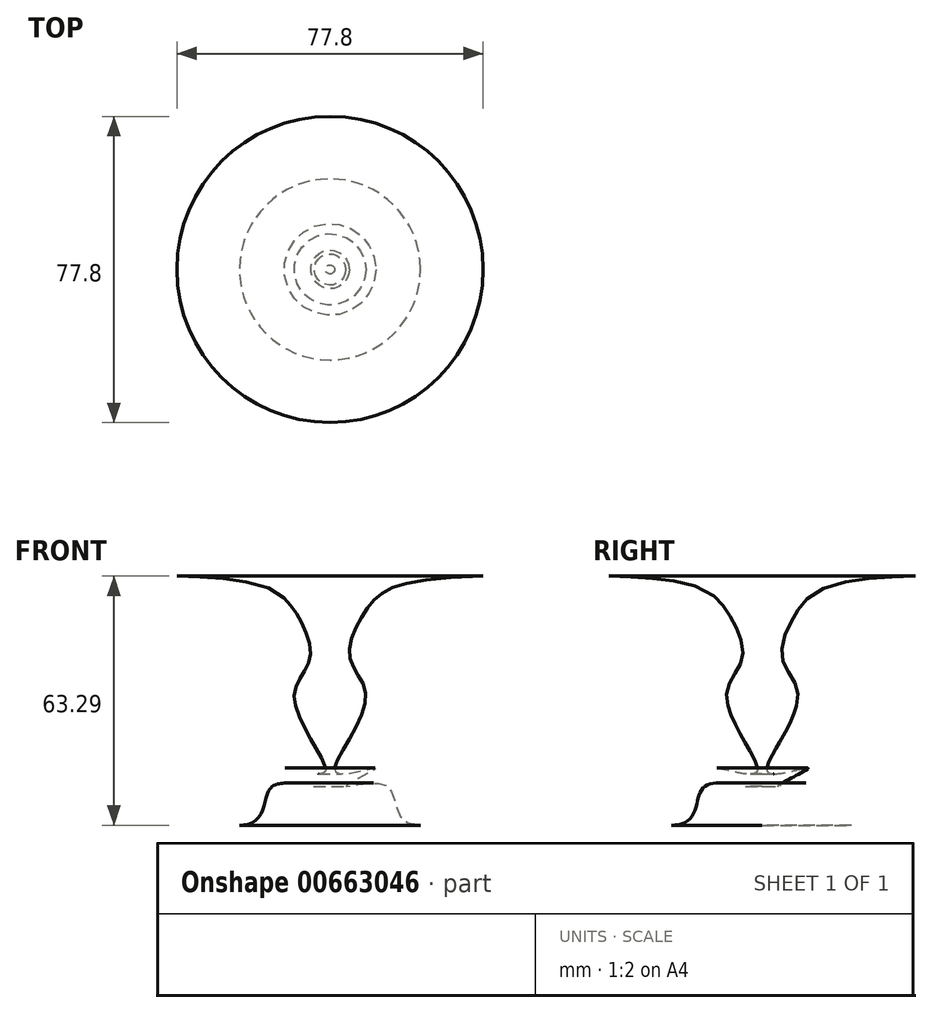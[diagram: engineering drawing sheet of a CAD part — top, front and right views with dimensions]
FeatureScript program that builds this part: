
annotation { "Feature Type Name" : "Feature", "Feature Type Description" : "" }
export const myFeature = defineFeature(function(context is Context, id is Id, definition is map)
    precondition{}
    {
        {
            var Q0;
            Q0=qCreatedBy(makeId("Front.planeOp"),FACE);
            var sketch = newSketch(context, id + "F0", { "sketchPlane" : qUnion([Q0])});
            skFitSpline(sketch, "E0", {"points": [v(38.9, 63.3) * mm, v(9.07, 54.53) * mm, v(5.04, 42.45) * mm, v(9.06, 33.53) * mm, v(2.65, 17.96) * mm, v(2.07, 13.12) * mm, v(11.64, 14.44) * mm, v(4, 9.97) * mm, v(14.45, 9.97) * mm, v(23, 0) * mm], "startDerivative": vector(-378.4, -11.1) * mm, "endDerivative": vector(208.34, 0) * mm});
            skLineSegment(sketch, "E1", {"start": v(0, 0) * mm, "end": v(0, 68.35) * mm, "construction": true});
            skLineSegment(sketch, "E2", {"start": v(0, 63.3) * mm, "end": v(38.9, 63.3) * mm});
            skLineSegment(sketch, "E3", {"start": v(0, 0) * mm, "end": v(23, 0) * mm});
            skPoint(sketch, "E4.orphan", {"position": v(-38.9, 63.3) * mm});
            skPoint(sketch, "E5.orphan", {"position": v(-23, 0) * mm});
            skLineSegment(sketch, "E6", {"start": v(0, 63.3) * mm, "end": v(0, 0) * mm});
            skSolve(sketch);
        }
        {
            var Q0;
            Q0=makeQuery(id+"F0.imprint","IMPRINT",FACE,{"disambiguationData":[TD([[makeQuery(id+"F0.imprint","IMPRINT",EDGE,{"derivedFrom":sQuery(id+"F0.wireOp",EDGE,"E0")}),-1.0]])]});
            var Q1;
            Q1=sQuery(id+"F0.wireOp",EDGE,"E6");
            revolve(context, id + "F1", {"entities" : qUnion([Q0]), "axis" : qUnion([Q1]), "revolveType" : RevolveType.FULL});
        }
    });
